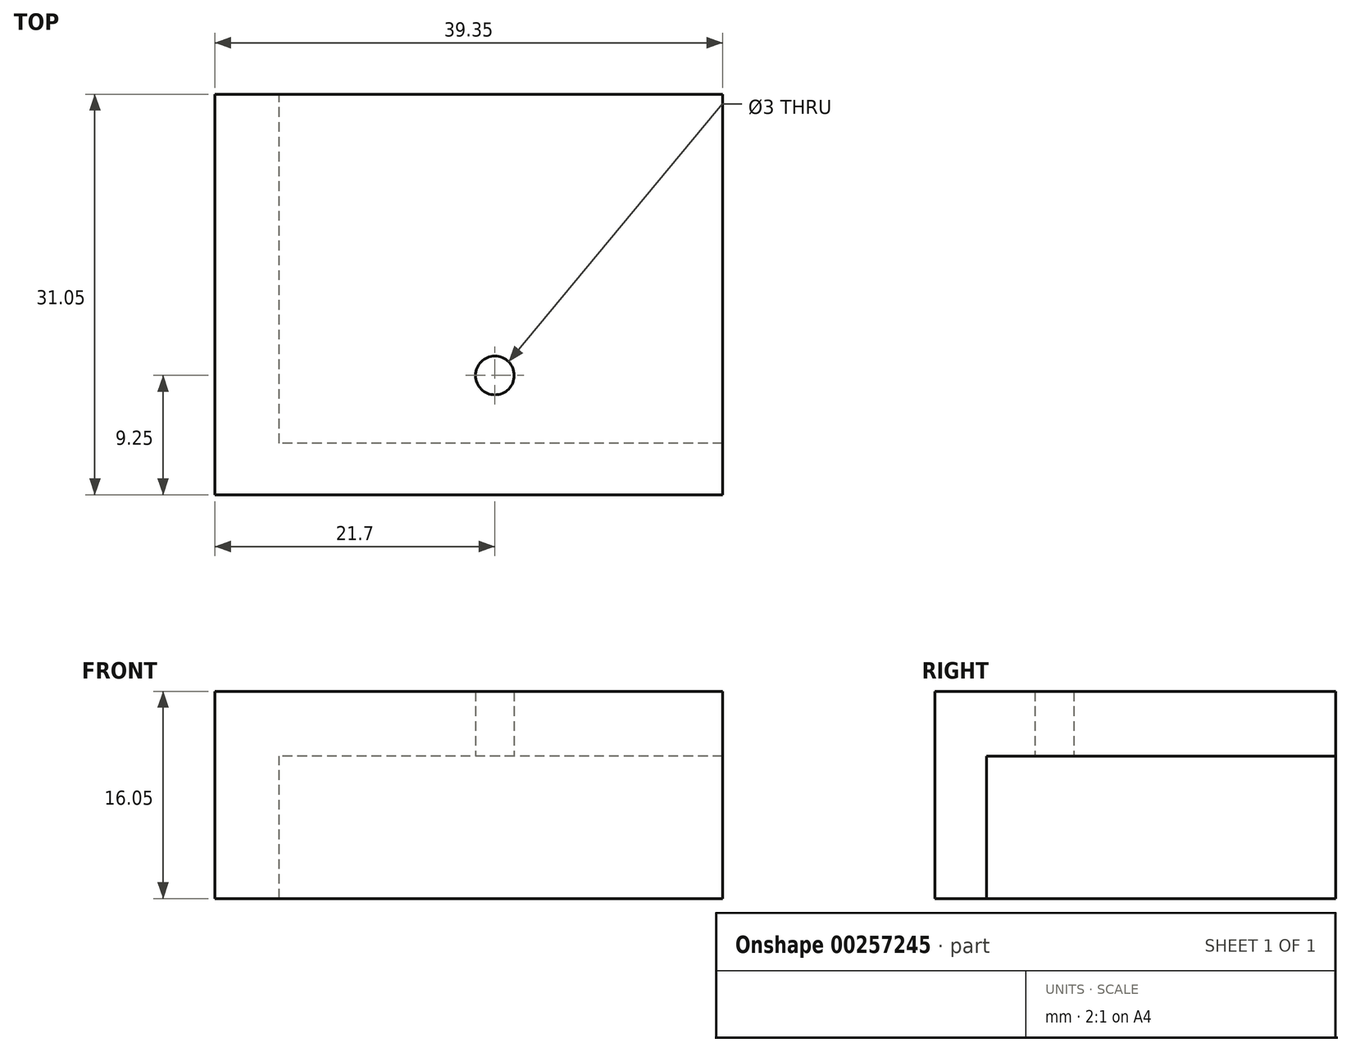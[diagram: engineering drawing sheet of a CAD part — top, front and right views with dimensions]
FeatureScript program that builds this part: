
annotation { "Feature Type Name" : "Feature", "Feature Type Description" : "" }
export const myFeature = defineFeature(function(context is Context, id is Id, definition is map)
    precondition{}
    {
        {
            var Q0;
            Q0=qCreatedBy(makeId("Top.planeOp"),FACE);
            var sketch = newSketch(context, id + "F0", { "sketchPlane" : qUnion([Q0])});
            skCircle(sketch, "E0", {"center": v(0, 0) * mm, "radius": 2.5 * mm, "construction": true});
            skLineSegment(sketch, "E1.bottom", {"start": v(10, 20) * mm, "end": v(-15.35, 20) * mm});
            skLineSegment(sketch, "E1.top", {"start": v(10, -11.05) * mm, "end": v(-15.35, -11.05) * mm});
            skLineSegment(sketch, "E1.left", {"start": v(10, 20) * mm, "end": v(10, -11.05) * mm});
            skLineSegment(sketch, "E1.right", {"start": v(-15.35, 20) * mm, "end": v(-15.35, -11.05) * mm});
            skLineSegment(sketch, "E2", {"start": v(-7.05, 20) * mm, "end": v(-7.05, -7.05) * mm, "construction": true});
            skLineSegment(sketch, "E3", {"start": v(-7.05, -7.05) * mm, "end": v(10, -7.05) * mm, "construction": true});
            skCircle(sketch, "E4", {"center": v(6.35, -1.8) * mm, "radius": 1.5 * mm});
            skSolve(sketch);
        }
        {
            var Q0;
            Q0=qSketchRegion(id+"F0",true);
            extrude(context, id + "F1", {"entities" : qUnion([Q0]), "depth" : 5 * mm});
        }
        {
            var Q0;
            Q0=makeQuery(id+"F1.opExtrude","CAP_FACE",FACE,{"disambiguationData":[OSD([sQuery(id+"F0.wireOp",EDGE,"E0"),sQuery(id+"F0.wireOp",EDGE,"E1.bottom"),sQuery(id+"F0.wireOp",EDGE,"E1.top"),sQuery(id+"F0.wireOp",EDGE,"E1.left"),sQuery(id+"F0.wireOp",EDGE,"E1.right")])],"isStart":false});
            var sketch = newSketch(context, id + "F2", { "sketchPlane" : qUnion([Q0])});
            skLineSegment(sketch, "E5", {"start": v(-15.35, 20) * mm, "end": v(-15.35, -11.05) * mm});
            skLineSegment(sketch, "E6", {"start": v(-15.35, -11.05) * mm, "end": v(10, -11.05) * mm});
            skLineSegment(sketch, "E7", {"start": v(10, -11.05) * mm, "end": v(10, -7.05) * mm});
            skLineSegment(sketch, "E8", {"start": v(10, -7.05) * mm, "end": v(-10.35, -7.05) * mm});
            skLineSegment(sketch, "E9", {"start": v(-10.35, -7.05) * mm, "end": v(-10.35, 20) * mm});
            skLineSegment(sketch, "E10", {"start": v(-10.35, 20) * mm, "end": v(-15.35, 20) * mm});
            skSolve(sketch);
        }
        {
            var Q0;
            Q0=qSketchRegion(id+"F2",true);
            extrude(context, id + "F3", {"entities" : qUnion([Q0]), "operationType" : NewBodyOperationType.ADD, "depth" : 8.55 * mm + 2.5 * mm});
        }
        {
            var Q0;
            Q0=makeQuery(id+"F3.boolean.opBoolean","MERGE",FACE,{"derivedFrom":[makeQuery(id+"F1.opExtrude","SWEPT_FACE",FACE,{"disambiguationData":[OSD([sQuery(id+"F0.wireOp",EDGE,"E1.left")])]}),makeQuery(id+"F3.opExtrude","SWEPT_FACE",FACE,{"disambiguationData":[OSD([sQuery(id+"F2.wireOp",EDGE,"E7")])]})]});
            var sketch = newSketch(context, id + "F4", { "sketchPlane" : qUnion([Q0])});
            skLineSegment(sketch, "E11", {"start": v(-11.05, 16.05) * mm, "end": v(-7.05, 16.05) * mm});
            skLineSegment(sketch, "E12", {"start": v(-7.05, 16.05) * mm, "end": v(-7.05, 5) * mm});
            skLineSegment(sketch, "E13", {"start": v(-7.05, 5) * mm, "end": v(20, 5) * mm});
            skLineSegment(sketch, "E14", {"start": v(20, 5) * mm, "end": v(20, 0) * mm});
            skLineSegment(sketch, "E15", {"start": v(20, 0) * mm, "end": v(-11.05, 0) * mm});
            skLineSegment(sketch, "E16", {"start": v(-11.05, 0) * mm, "end": v(-11.05, 16.05) * mm});
            skSolve(sketch);
        }
        {
            var Q0;
            Q0=qSketchRegion(id+"F4",true);
            extrude(context, id + "F5", {"entities" : qUnion([Q0]), "operationType" : NewBodyOperationType.ADD, "depth" : 14 * mm});
        }
        {
            var Q0;
            Q0=makeQuery(id+"F5.boolean.opBoolean","MERGE",FACE,{"derivedFrom":[makeQuery(id+"F3.opExtrude","CAP_FACE",FACE,{"disambiguationData":[OSD([sQuery(id+"F2.wireOp",EDGE,"E5"),sQuery(id+"F2.wireOp",EDGE,"E6"),sQuery(id+"F2.wireOp",EDGE,"E7"),sQuery(id+"F2.wireOp",EDGE,"E8"),sQuery(id+"F2.wireOp",EDGE,"E9"),sQuery(id+"F2.wireOp",EDGE,"E10")])],"isStart":false}),makeQuery(id+"F5.opExtrude","SWEPT_FACE",FACE,{"disambiguationData":[OSD([sQuery(id+"F4.wireOp",EDGE,"E11")])]})]});
            var sketch = newSketch(context, id + "F6", { "sketchPlane" : qUnion([Q0])});
            skLineSegment(sketch, "E17", {"start": v(-15.35, 20) * mm, "end": v(-10.35, 20) * mm});
            skLineSegment(sketch, "E18", {"start": v(-10.35, 20) * mm, "end": v(-10.35, -7.05) * mm});
            skLineSegment(sketch, "E19", {"start": v(-10.35, -7.05) * mm, "end": v(24, -7.05) * mm});
            skLineSegment(sketch, "E20", {"start": v(24, -7.05) * mm, "end": v(24, -11.05) * mm});
            skLineSegment(sketch, "E21", {"start": v(24, -11.05) * mm, "end": v(-15.35, -11.05) * mm});
            skLineSegment(sketch, "E22", {"start": v(-15.35, -11.05) * mm, "end": v(-15.35, 20) * mm});
            skSolve(sketch);
        }
        {
            var Q0;
            Q0 = qSketchRegion(id + "F6", true);
            extrude(context, id + "F7", {"entities" : qUnion([Q0]), "operationType" : NewBodyOperationType.ADD, "oppositeDirection" : true, "depth" : 8.55 * mm + 2.5 * mm + 8.55 * mm + 2.5 * mm + 5 * mm});
        }
        {
            var Q0;
            Q0=makeQuery(id+"F5.boolean.opBoolean","MERGE",FACE,{"derivedFrom":[makeQuery(id+"F3.opExtrude","CAP_FACE",FACE,{"disambiguationData":[OSD([sQuery(id+"F2.wireOp",EDGE,"E5"),sQuery(id+"F2.wireOp",EDGE,"E6"),sQuery(id+"F2.wireOp",EDGE,"E7"),sQuery(id+"F2.wireOp",EDGE,"E8"),sQuery(id+"F2.wireOp",EDGE,"E9"),sQuery(id+"F2.wireOp",EDGE,"E10")])],"isStart":false}),makeQuery(id+"F5.opExtrude","SWEPT_FACE",FACE,{"disambiguationData":[OSD([sQuery(id+"F4.wireOp",EDGE,"E11")])]})]});
            var sketch = newSketch(context, id + "F8", { "sketchPlane" : qUnion([Q0])});
            skLineSegment(sketch, "E23", {"start": v(-15.35, 20) * mm, "end": v(-10.35, 20) * mm});
            skLineSegment(sketch, "E24", {"start": v(-10.35, 20) * mm, "end": v(-10.35, -7.05) * mm});
            skLineSegment(sketch, "E25", {"start": v(-10.35, -7.05) * mm, "end": v(24, -7.05) * mm});
            skLineSegment(sketch, "E26", {"start": v(24, -7.05) * mm, "end": v(24, -11.05) * mm});
            skLineSegment(sketch, "E27", {"start": v(24, -11.05) * mm, "end": v(-15.35, -11.05) * mm});
            skLineSegment(sketch, "E28", {"start": v(-15.35, -11.05) * mm, "end": v(-15.35, 20) * mm});
            skSolve(sketch);
        }
        {
            var Q0;
            Q0 = qSketchRegion(id + "F8", true);
            extrude(context, id + "F9", {"entities" : qUnion([Q0]), "operationType" : NewBodyOperationType.REMOVE, "oppositeDirection" : true, "depth" : 8.55 * mm + 2.5 * mm});
        }
    });
